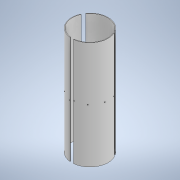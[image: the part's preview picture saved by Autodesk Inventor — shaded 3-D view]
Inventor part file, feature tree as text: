
AUTODESK INVENTOR PART (.ipt)
format: ipt  version: 2021 (Build 250183000, 183)  size: 263,680 bytes
history: native  units: in
note: dims shown in document units (in); Inventor stores cm internally (conversion verified against a paired STEP export)
features: other x28, hole x7, pattern_circular x6, sketch x6, plane x5, extrude x2
ambient origin geometry x8: Origin, YZ Plane, XZ Plane, XY Plane, X Axis, Y Axis, Z Axis, Center Point
bodies: Solid1 (feature_tree)
feature tree (54):
  extrude  "Extrusion1"  TaperAngle=0.0deg  [1 undecoded]
  plane  "Work Plane1"
  extrude  "Extrusion2"  Depth=0.3937in TaperAngle=0.0deg
  pattern_circular  "Circular Pattern1"  Count=3 Angle=360.0deg
  other  "Work Axis1"
  other  "Work Axis2"
  other  "Work Axis3"
  other  "Work Axis4"
  other  "Work Point1"
  other  "Work Point2"
  other  "Work Point3"
  other  "Central Plane"
  other  "Work Point4"
  other  "Work Axis6"
  other  "Work Axis7"
  other  "Offset Plane A"
  other  "Work Point5"
  other  "Work Point6"
  other  "Work Axis8"
  other  "Work Axis9"
  other  "Work Point7"
  other  "Work Point8"
  plane  "Work Plane5"
  plane  "Work Plane6"
  hole  "Hole1"  [1 undecoded]
  hole  "Hole2"  [1 undecoded]
  pattern_circular  "Circular Pattern3"  Count=3 Angle=360.0deg
  sketch  "Sketch5"  dims[d13=0.0484in d14=-11.811in]
  plane  "Work Plane7"
  sketch  "Sketch6"  dims[d15=0.0484in d16=0.1574in]
  hole  "Hole3"  [1 undecoded]
  other  "Work Axis10"
  hole  "Hole4"  [1 undecoded]
  pattern_circular  "Circular Pattern5"  Count=4 Angle=360.0deg
  plane  "Work Plane12"
  hole  "Hole5"  [1 undecoded]
  pattern_circular  "Circular Pattern6"  Count=3 Angle=360.0deg
  other  "plane for insert hole 1"
  sketch  "Sketch7"  dims[d17=-0.1574in]
  other  "plane for insert hole 2"
  hole  "insert hole 2"  [1 undecoded]
  hole  "insert hole 1"  [1 undecoded]
  pattern_circular  "Circular Pattern7"  [2 undecoded]
  pattern_circular  "Circular Pattern9"  [2 undecoded]
  sketch  "Sketch1"  dims[d3=0.0in d5=0.0in]
  sketch  "Sketch2"  dims[d7=0.3937in d8=0.5in d9=0.0in d10=1.1811in d11=360.0deg]
  other  "Work Axis5"
  other  "Offset Plane B"
  other  "Work Axis11"
  other  "Work Axis12"
  other  "Work Point9"
  other  "Work Axis13"
  other  "Work Point10"
  sketch  "Sketch8"  dims[d48=1.0in d49=1.0in d29=0.096in d30=0.75in d31=0.185in d32=0.25in d33=0.5635in d34=1.0in d35=0.0in d52=1.0in d53=1.0in d38=0.096in d39=0.75in d40=0.185in d41=0.25in d42=0.5635in d43=1.0in d44=0.8108in d45=1.1811in d46=360.0deg d51=0.38in d54=0.177in d55=0.328in d56=0.332in d57=0.25in d58=0.5635in d59=0.484in d60=0.8108in d64=0.19in d65=0.177in d66=0.3229in d67=0.332in d68=0.25in d69=0.5635in d70=0.484in d71=0.8108in d72=1.5748in d73=360.0deg d75=60.0deg d76=1.0in d77=1.0in d78=0.129in d79=0.3229in d80=0.225in d81=0.25in d82=0.5635in d83=0.484in d84=0.8108in d85=1.1811in d86=360.0deg d88=0.2749in d89=0.2749in d90=0.0in d91=0.0in d92=0.0in d93=11.811in d94=0.0in d95=11.811in d96=0.129in d97=0.224in d98=0.225in d99=0.25in d100=0.5635in d101=0.349in d102=0.8108in d103=0.129in d104=0.224in d105=0.225in d106=0.25in d107=0.5635in d108=0.349in d109=0.8108in d110=1.1811in d111=360.0deg d116=1.1811in d117=360.0deg d119=0.0in d61=0.75in d62=0.8108in d63=0.0625in]
note: 12 required parameter values undecoded (feature->parameter linkage not recoverable at this tier; creation-order binding heuristic only, values carry confidence <= 0.55)
